# Revit family: APX40TN
name_source: partatom
category: Communication Devices
revit_build: Autodesk Revit 2014 (Build: 20140709_2115(x64)
units: mm (PartAtom-declared; Revit-internal decimal feet)

## types (1)
- Horn Loudspeaker
    100V Taps = 5.0, 10.0, 20.0, 40.0
    25V Taps = .63, 1.25, 2.5, 3.75, 5.0, 10.0, 20.0, 40.0
    70V Taps = 2.5, 5.0, 10.0, 20.0, 30.0, 40.0
    Baffle Material = <By Category>
    Body Material = QF_Plastic - White - Smooth
    Color = <By Category>
    Cost = 135.99 $
    Cost MSRP = 135.99 $
    Coverage Vertical = 0.00°
    Depth = 13 1/4"
    Description = CONSTANT-DIRECTIVITY 40W PAGING SPEAKER W ROTATING BELL
    Dispersion Angle = 60.00°
    Enclosure Material = <By Category>
    Family Code (default) = LOUD SPEAKERS
    Frequency Response  = 400 - 7500Hz
    Grill Material = <By Category>
    Height = 10 1/4"
    IQ Category = SPEAKERS
    Ingress Protection = IP-34
    Input Connectors = Barrier Terminal
    Manufacturer = ATLAS SOUND
    Manufacturer URL = https://www.atlasied.com
    Market = Commercial, Higher Education, Emergency
    MasterFormat = 27 41 13
    MaterFormat Title = SPEAKERS
    Model = APX40TN
    OmniClass Number = 23-37 17 13 19
    OmniClass Title = SPEAKERS
    Part Number = APX40TN
    Pitch = 0.00°
    Power Peak = 124
    Power Rating (RMS) = 40 Watts
    Product Documentation Link = https://www.atlasied.com
    Product Page URL = https://www.atlasied.com
    Rotation = 0.00°
    SPL Max = 107
    ScheduleType |RF| = AtlasIED Master
    Sensitivity = 107
    Speaker Dispersion = 60.00°
    Transformer Option = Yes
    URL = www.atlassound.com
    Vertical Symmetry = Yes
    Warranty = 5 Year
    Weight Product = 9
    Width = 14 1/2"

## geometry (parser evidence)
native form markers: Blend x6, Sweep x4
no freeform markers — native parametric forms only
